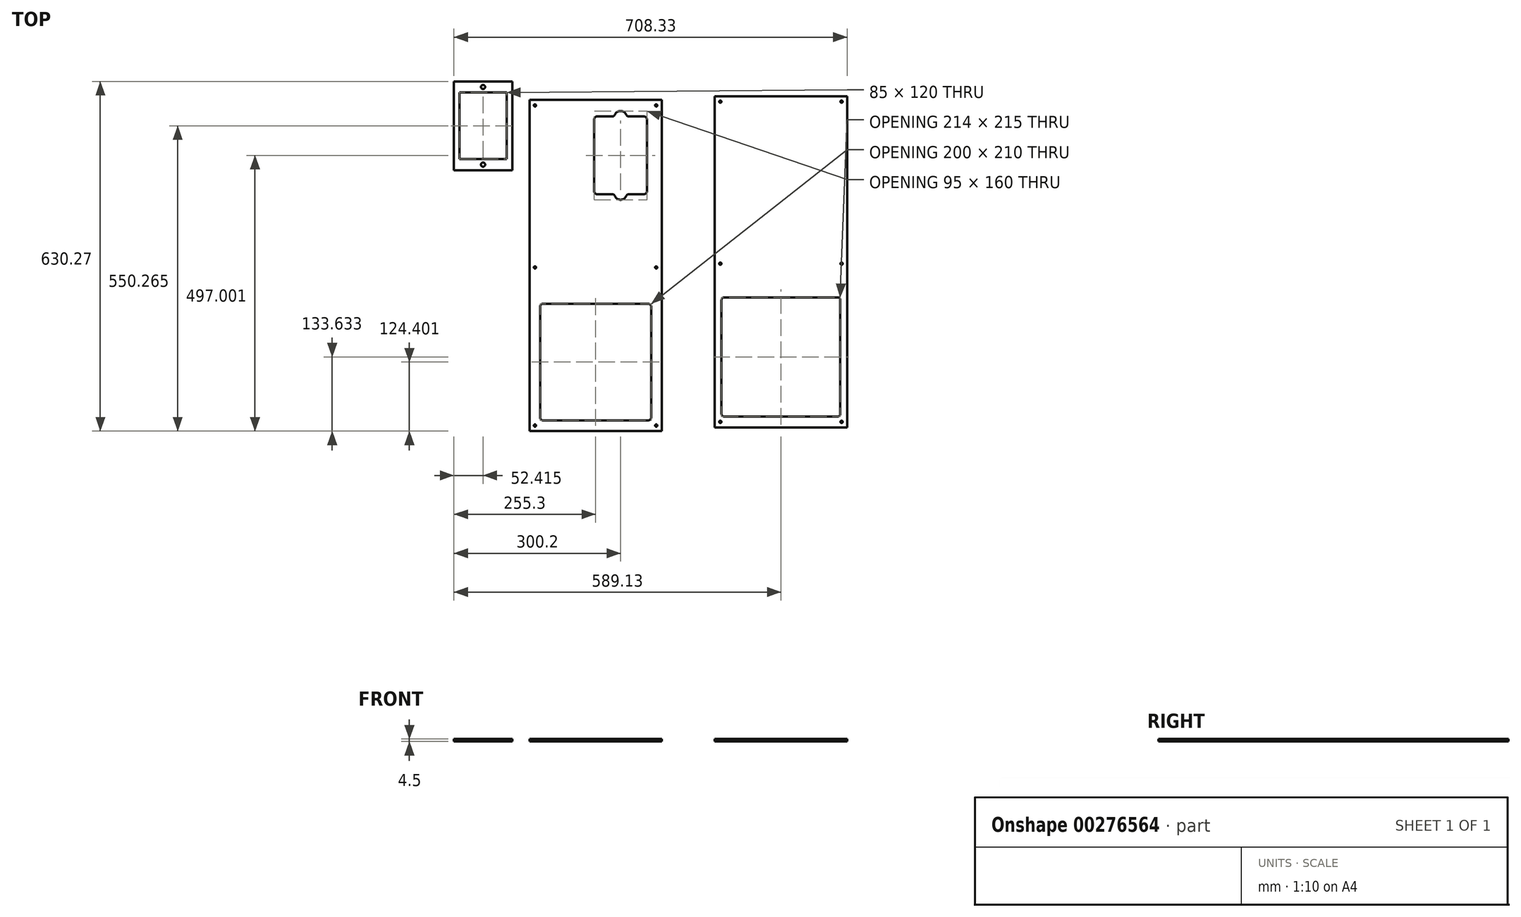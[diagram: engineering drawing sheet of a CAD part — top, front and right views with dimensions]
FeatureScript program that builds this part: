
annotation { "Feature Type Name" : "Feature", "Feature Type Description" : "" }
export const myFeature = defineFeature(function(context is Context, id is Id, definition is map)
    precondition{}
    {
        {
            var Q0;
            Q0=qCreatedBy(makeId("Top.planeOp"),FACE);
            var sketch = newSketch(context, id + "F0", { "sketchPlane" : qUnion([Q0])});
            skLineSegment(sketch, "E0.bottom", {"start": v(-206, 398.8) * mm, "end": v(32.4, 398.8) * mm});
            skLineSegment(sketch, "E0.top", {"start": v(-206, -198.2) * mm, "end": v(32.4, -198.2) * mm});
            skLineSegment(sketch, "E0.left", {"start": v(-206, 398.8) * mm, "end": v(-206, -198.2) * mm});
            skLineSegment(sketch, "E0.right", {"start": v(32.4, 398.8) * mm, "end": v(32.4, -198.2) * mm});
            skLineSegment(sketch, "E1.bottom", {"start": v(-186.8, 31.2) * mm, "end": v(13.2, 31.2) * mm});
            skLineSegment(sketch, "E1.top", {"start": v(-186.8, -178.8) * mm, "end": v(13.2, -178.8) * mm});
            skLineSegment(sketch, "E1.left", {"start": v(-186.8, 31.2) * mm, "end": v(-186.8, -178.8) * mm});
            skLineSegment(sketch, "E1.right", {"start": v(13.2, 31.2) * mm, "end": v(13.2, -178.8) * mm});
            skLineSegment(sketch, "E2.bottom", {"start": v(-89.4, 368.8) * mm, "end": v(5.6, 368.8) * mm});
            skLineSegment(sketch, "E2.top", {"start": v(-89.4, 228.8) * mm, "end": v(5.6, 228.8) * mm});
            skLineSegment(sketch, "E2.left", {"start": v(-89.4, 368.8) * mm, "end": v(-89.4, 228.8) * mm});
            skLineSegment(sketch, "E2.right", {"start": v(5.6, 368.8) * mm, "end": v(5.6, 228.8) * mm});
            skCircle(sketch, "E3", {"center": v(-49.48, 368.8) * mm, "radius": 3.2 * mm});
            skSolve(sketch);
        }
        {
            var Q0;
            Q0 = qSketchRegion(id + "F0", true);
            extrude(context, id + "F1", {"entities" : qUnion([Q0]), "depth" : 4.5 * mm, "offsetDistance" : 25 * mm});
        }
        {
            var Q0;
            Q0=makeQuery(id+"F1.opExtrude","CAP_FACE",FACE,{"disambiguationData":[OSD([sQuery(id+"F0.wireOp",EDGE,"E0.bottom"),sQuery(id+"F0.wireOp",EDGE,"E0.top"),sQuery(id+"F0.wireOp",EDGE,"E0.left"),sQuery(id+"F0.wireOp",EDGE,"E0.right"),sQuery(id+"F0.wireOp",EDGE,"E1.bottom"),sQuery(id+"F0.wireOp",EDGE,"E1.top"),sQuery(id+"F0.wireOp",EDGE,"E1.left"),sQuery(id+"F0.wireOp",EDGE,"E1.right"),sQuery(id+"F0.wireOp",EDGE,"E2.bottom"),sQuery(id+"F0.wireOp",EDGE,"E2.top"),sQuery(id+"F0.wireOp",EDGE,"E2.left"),sQuery(id+"F0.wireOp",EDGE,"E2.right"),sQuery(id+"F0.wireOp",EDGE,"f5iPQAOY-qOqS-fJNy-qLz2-Z3B5W6fyXTsv"),sQuery(id+"F0.wireOp",EDGE,"IoBfbX9C-VoXT-43uz-JrJR-B73ar7WCOE58")])],"isStart":false});
            var sketch = newSketch(context, id + "F2", { "sketchPlane" : qUnion([Q0])});
            skPoint(sketch, "E4", {"position": v(-196, -188.2) * mm});
            skPoint(sketch, "E5", {"position": v(22.4, -188.2) * mm});
            skPoint(sketch, "E6", {"position": v(22.4, 96.8) * mm});
            skPoint(sketch, "E7", {"position": v(22.4, 388.8) * mm});
            skPoint(sketch, "E8", {"position": v(-196, 96.8) * mm});
            skPoint(sketch, "E9", {"position": v(-196, 388.8) * mm});
            skSolve(sketch);
        }
        {
            var Q0;
            Q0=sQuery(id+"F2.wireOp",VERTEX,"E9");
            var Q1;
            Q1=sQuery(id+"F2.wireOp",VERTEX,"E7");
            var Q2;
            Q2=sQuery(id+"F2.wireOp",VERTEX,"E6");
            var Q3;
            Q3=sQuery(id+"F2.wireOp",VERTEX,"E8");
            var Q4;
            Q4=sQuery(id+"F2.wireOp",VERTEX,"E4");
            var Q5;
            Q5=sQuery(id+"F2.wireOp",VERTEX,"E5");
            var Q6;
            Q6=makeQuery(id+"F1.opExtrude","SWEPT_BODY",BODY,{"disambiguationData":[OSD([sQuery(id+"F0.wireOp",EDGE,"E0.bottom"),sQuery(id+"F0.wireOp",EDGE,"E0.top"),sQuery(id+"F0.wireOp",EDGE,"E0.left"),sQuery(id+"F0.wireOp",EDGE,"E0.right"),sQuery(id+"F0.wireOp",EDGE,"E1.bottom"),sQuery(id+"F0.wireOp",EDGE,"E1.top"),sQuery(id+"F0.wireOp",EDGE,"E1.left"),sQuery(id+"F0.wireOp",EDGE,"E1.right"),sQuery(id+"F0.wireOp",EDGE,"E2.bottom"),sQuery(id+"F0.wireOp",EDGE,"E2.top"),sQuery(id+"F0.wireOp",EDGE,"E2.left"),sQuery(id+"F0.wireOp",EDGE,"E2.right"),sQuery(id+"F0.wireOp",EDGE,"f5iPQAOY-qOqS-fJNy-qLz2-Z3B5W6fyXTsv"),sQuery(id+"F0.wireOp",EDGE,"IoBfbX9C-VoXT-43uz-JrJR-B73ar7WCOE58")])]});
            hole(context, id + "F3", {"style" : HoleStyle.SIMPLE, "endStyle" : HoleEndStyle.THROUGH, "holeDiameter" : 4 * mm, "majorDiameter" : 5 * mm, "tappedDepth" : 12 * mm, "tapClearance" : 3, "locations" : qUnion([Q0, Q1, Q2, Q3, Q4, Q5]), "scope" : qUnion([Q6])});
        }
        {
            var Q0;
            Q0=qCreatedBy(makeId("Top.planeOp"),FACE);
            var sketch = newSketch(context, id + "F4", { "sketchPlane" : qUnion([Q0])});
            skLineSegment(sketch, "E10.bottom", {"start": v(127.83, 405.53) * mm, "end": v(366.23, 405.53) * mm});
            skLineSegment(sketch, "E10.top", {"start": v(127.83, -191.47) * mm, "end": v(366.23, -191.47) * mm});
            skLineSegment(sketch, "E10.left", {"start": v(127.83, 405.53) * mm, "end": v(127.83, -191.47) * mm});
            skLineSegment(sketch, "E10.right", {"start": v(366.23, 405.53) * mm, "end": v(366.23, -191.47) * mm});
            skLineSegment(sketch, "E11.bottom", {"start": v(140.03, 42.93) * mm, "end": v(354.03, 42.93) * mm});
            skLineSegment(sketch, "E11.top", {"start": v(140.03, -172.07) * mm, "end": v(354.03, -172.07) * mm});
            skLineSegment(sketch, "E11.left", {"start": v(140.03, 42.93) * mm, "end": v(140.03, -172.07) * mm});
            skLineSegment(sketch, "E11.right", {"start": v(354.03, 42.93) * mm, "end": v(354.03, -172.07) * mm});
            skPoint(sketch, "E12", {"position": v(137.83, 103.53) * mm});
            skSolve(sketch);
        }
        {
            var Q0;
            Q0 = qSketchRegion(id + "F4", true);
            extrude(context, id + "F5", {"entities" : qUnion([Q0]), "depth" : 4.5 * mm, "offsetDistance" : 25 * mm});
        }
        {
            var Q0;
            Q0=makeQuery(id+"F5.opExtrude","CAP_FACE",FACE,{"disambiguationData":[OSD([sQuery(id+"F4.wireOp",EDGE,"E10.bottom"),sQuery(id+"F4.wireOp",EDGE,"E10.top"),sQuery(id+"F4.wireOp",EDGE,"E10.left"),sQuery(id+"F4.wireOp",EDGE,"E10.right"),sQuery(id+"F4.wireOp",EDGE,"E11.bottom"),sQuery(id+"F4.wireOp",EDGE,"E11.top"),sQuery(id+"F4.wireOp",EDGE,"E11.left"),sQuery(id+"F4.wireOp",EDGE,"E11.right")])],"isStart":false});
            var sketch = newSketch(context, id + "F6", { "sketchPlane" : qUnion([Q0])});
            skPoint(sketch, "E13", {"position": v(137.83, 395.53) * mm});
            skPoint(sketch, "E14", {"position": v(356.23, 395.53) * mm});
            skPoint(sketch, "E15", {"position": v(356.23, 103.53) * mm});
            skPoint(sketch, "E16", {"position": v(356.23, -181.47) * mm});
            skPoint(sketch, "E17", {"position": v(137.83, -181.47) * mm});
            skPoint(sketch, "E18", {"position": v(137.83, 103.53) * mm});
            skSolve(sketch);
        }
        {
            var Q0;
            Q0=sQuery(id+"F6.wireOp",VERTEX,"E13");
            var Q1;
            Q1=sQuery(id+"F6.wireOp",VERTEX,"E14");
            var Q2;
            Q2=sQuery(id+"F6.wireOp",VERTEX,"E15");
            var Q3;
            Q3=sQuery(id+"F6.wireOp",VERTEX,"E18");
            var Q4;
            Q4=sQuery(id+"F6.wireOp",VERTEX,"E17");
            var Q5;
            Q5=sQuery(id+"F6.wireOp",VERTEX,"E16");
            var Q6;
            Q6=makeQuery(id+"F5.opExtrude","SWEPT_BODY",BODY,{"disambiguationData":[OSD([sQuery(id+"F4.wireOp",EDGE,"E10.bottom"),sQuery(id+"F4.wireOp",EDGE,"E10.top"),sQuery(id+"F4.wireOp",EDGE,"E10.left"),sQuery(id+"F4.wireOp",EDGE,"E10.right"),sQuery(id+"F4.wireOp",EDGE,"E11.bottom"),sQuery(id+"F4.wireOp",EDGE,"E11.top"),sQuery(id+"F4.wireOp",EDGE,"E11.left"),sQuery(id+"F4.wireOp",EDGE,"E11.right")])]});
            hole(context, id + "F7", {"style" : HoleStyle.SIMPLE, "endStyle" : HoleEndStyle.THROUGH, "holeDiameter" : 4 * mm, "majorDiameter" : 5 * mm, "tappedDepth" : 12 * mm, "tapClearance" : 3, "locations" : qUnion([Q0, Q1, Q2, Q3, Q4, Q5]), "scope" : qUnion([Q6])});
        }
        {
            var Q0;
            Q0=makeQuery(id+"F5.opExtrude","SWEPT_EDGE",EDGE,{"disambiguationData":[OSD([sQuery(id+"F4.wireOp",EDGE,"E11.bottom"),sQuery(id+"F4.wireOp",EDGE,"E11.right")])]});
            var Q1;
            Q1=makeQuery(id+"F5.opExtrude","SWEPT_EDGE",EDGE,{"disambiguationData":[OSD([sQuery(id+"F4.wireOp",EDGE,"E11.bottom"),sQuery(id+"F4.wireOp",EDGE,"E11.left")])]});
            var Q2;
            Q2=makeQuery(id+"F5.opExtrude","SWEPT_EDGE",EDGE,{"disambiguationData":[OSD([sQuery(id+"F4.wireOp",EDGE,"E11.top"),sQuery(id+"F4.wireOp",EDGE,"E11.right")])]});
            var Q3;
            Q3=makeQuery(id+"F5.opExtrude","SWEPT_EDGE",EDGE,{"disambiguationData":[OSD([sQuery(id+"F4.wireOp",EDGE,"E11.top"),sQuery(id+"F4.wireOp",EDGE,"E11.left")])]});
            fillet(context, id + "F8", {"entities" : qUnion([Q0, Q1, Q2, Q3]), "radius" : 5 * mm, "tangentPropagation" : true, "allowEdgeOverflow" : false});
        }
        {
            var Q0;
            Q0=makeQuery(id+"F1.opExtrude","SWEPT_EDGE",EDGE,{"disambiguationData":[OSD([sQuery(id+"F0.wireOp",EDGE,"E1.bottom"),sQuery(id+"F0.wireOp",EDGE,"E1.right")])]});
            var Q1;
            Q1=makeQuery(id+"F1.opExtrude","SWEPT_EDGE",EDGE,{"disambiguationData":[OSD([sQuery(id+"F0.wireOp",EDGE,"E1.bottom"),sQuery(id+"F0.wireOp",EDGE,"E1.left")])]});
            var Q2;
            Q2=makeQuery(id+"F1.opExtrude","SWEPT_EDGE",EDGE,{"disambiguationData":[OSD([sQuery(id+"F0.wireOp",EDGE,"E1.top"),sQuery(id+"F0.wireOp",EDGE,"E1.right")])]});
            var Q3;
            Q3=makeQuery(id+"F1.opExtrude","SWEPT_EDGE",EDGE,{"disambiguationData":[OSD([sQuery(id+"F0.wireOp",EDGE,"E1.top"),sQuery(id+"F0.wireOp",EDGE,"E1.left")])]});
            fillet(context, id + "F9", {"entities" : qUnion([Q0, Q1, Q2, Q3]), "radius" : 5 * mm, "tangentPropagation" : true, "allowEdgeOverflow" : false});
        }
        {
            var Q0;
            Q0=makeQuery(id+"F1.opExtrude","SWEPT_EDGE",EDGE,{"disambiguationData":[OSD([sQuery(id+"F0.wireOp",EDGE,"E2.bottom"),sQuery(id+"F0.wireOp",EDGE,"E2.left")])]});
            var Q1;
            Q1=makeQuery(id+"F1.opExtrude","SWEPT_EDGE",EDGE,{"disambiguationData":[OSD([sQuery(id+"F0.wireOp",EDGE,"E2.bottom"),sQuery(id+"F0.wireOp",EDGE,"E2.right")])]});
            var Q2;
            Q2=makeQuery(id+"F1.opExtrude","SWEPT_EDGE",EDGE,{"disambiguationData":[OSD([sQuery(id+"F0.wireOp",EDGE,"E2.top"),sQuery(id+"F0.wireOp",EDGE,"E2.right")])]});
            var Q3;
            Q3=makeQuery(id+"F1.opExtrude","SWEPT_EDGE",EDGE,{"disambiguationData":[OSD([sQuery(id+"F0.wireOp",EDGE,"E2.top"),sQuery(id+"F0.wireOp",EDGE,"E2.left")])]});
            fillet(context, id + "F10", {"entities" : qUnion([Q0, Q1, Q2, Q3]), "tangentPropagation" : true, "radius" : 5 * mm, "defaultsChanged" : false, "vertexSettings" : [], "allowEdgeOverflow" : false});
        }
        {
            var Q0;
            Q0=qCreatedBy(makeId("Top.planeOp"),FACE);
            var sketch = newSketch(context, id + "F11", { "sketchPlane" : qUnion([Q0])});
            skLineSegment(sketch, "E19.bottom", {"start": v(-342.1, 432.07) * mm, "end": v(-237.1, 432.07) * mm});
            skLineSegment(sketch, "E19.top", {"start": v(-342.1, 272.07) * mm, "end": v(-237.1, 272.07) * mm});
            skLineSegment(sketch, "E19.left", {"start": v(-342.1, 432.07) * mm, "end": v(-342.1, 272.07) * mm});
            skLineSegment(sketch, "E19.right", {"start": v(-237.1, 432.07) * mm, "end": v(-237.1, 272.07) * mm});
            skSolve(sketch);
        }
        {
            var Q0;
            Q0=makeQuery(id+"F11.imprint","IMPRINT",FACE,{"disambiguationData":[TD([[makeQuery(id+"F11.imprint","IMPRINT",EDGE,{"derivedFrom":sQuery(id+"F11.wireOp",EDGE,"E19.bottom")}),-1.0]])]});
            extrude(context, id + "F12", {"entities" : qUnion([Q0]), "depth" : 4.5 * mm, "offsetDistance" : 25 * mm});
        }
        {
            var Q0;
            Q0=makeQuery(id+"F12.opExtrude","CAP_FACE",FACE,{"disambiguationData":[OSD([sQuery(id+"F11.wireOp",EDGE,"E19.bottom"),sQuery(id+"F11.wireOp",EDGE,"E19.top"),sQuery(id+"F11.wireOp",EDGE,"E19.left"),sQuery(id+"F11.wireOp",EDGE,"E19.right")])],"isStart":false});
            var sketch = newSketch(context, id + "F13", { "sketchPlane" : qUnion([Q0])});
            skLineSegment(sketch, "E20.bottom", {"start": v(-332.18, 412.07) * mm, "end": v(-247.18, 412.07) * mm});
            skLineSegment(sketch, "E20.top", {"start": v(-332.18, 292.07) * mm, "end": v(-247.18, 292.07) * mm});
            skLineSegment(sketch, "E20.left", {"start": v(-332.18, 412.07) * mm, "end": v(-332.18, 292.07) * mm});
            skLineSegment(sketch, "E20.right", {"start": v(-247.18, 412.07) * mm, "end": v(-247.18, 292.07) * mm});
            skCircle(sketch, "E21", {"center": v(-289.6, 422.07) * mm, "radius": 3.75 * mm});
            skPoint(sketch, "E21.centerSnap0", {"position": v(-289.6, 432.07) * mm});
            skCircle(sketch, "E22", {"center": v(-289.6, 282.07) * mm, "radius": 3.75 * mm});
            skSolve(sketch);
        }
        {
            var Q0;
            Q0 = qSketchRegion(id + "F13", true);
            extrude(context, id + "F14", {"entities" : qUnion([Q0]), "operationType" : NewBodyOperationType.REMOVE, "oppositeDirection" : true, "depth" : 25 * mm, "offsetDistance" : 25 * mm});
        }
        {
            var Q0;
            Q0=makeQuery(id+"F1.opExtrude","CAP_FACE",FACE,{"disambiguationData":[OSD([sQuery(id+"F0.wireOp",EDGE,"E0.bottom"),sQuery(id+"F0.wireOp",EDGE,"E0.top"),sQuery(id+"F0.wireOp",EDGE,"E0.left"),sQuery(id+"F0.wireOp",EDGE,"E0.right"),sQuery(id+"F0.wireOp",EDGE,"E1.bottom"),sQuery(id+"F0.wireOp",EDGE,"E1.top"),sQuery(id+"F0.wireOp",EDGE,"E1.left"),sQuery(id+"F0.wireOp",EDGE,"E1.right"),sQuery(id+"F0.wireOp",EDGE,"E2.bottom"),sQuery(id+"F0.wireOp",EDGE,"E2.top"),sQuery(id+"F0.wireOp",EDGE,"E2.left"),sQuery(id+"F0.wireOp",EDGE,"E2.right"),sQuery(id+"F0.wireOp",EDGE,"E3")])],"isStart":false});
            var sketch = newSketch(context, id + "F15", { "sketchPlane" : qUnion([Q0])});
            skLineSegment(sketch, "E23.bottom", {"start": v(-52.9, 378.8) * mm, "end": v(-30.9, 378.8) * mm});
            skLineSegment(sketch, "E23.top", {"start": v(-52.9, 218.8) * mm, "end": v(-30.9, 218.8) * mm});
            skLineSegment(sketch, "E23.left", {"start": v(-52.9, 378.8) * mm, "end": v(-52.9, 218.8) * mm});
            skLineSegment(sketch, "E23.right", {"start": v(-30.9, 378.8) * mm, "end": v(-30.9, 218.8) * mm});
            skSolve(sketch);
        }
        {
            var Q0;
            Q0 = qSketchRegion(id + "F15", true);
            extrude(context, id + "F16", {"entities" : qUnion([Q0]), "operationType" : NewBodyOperationType.REMOVE, "oppositeDirection" : true, "depth" : 25 * mm, "offsetDistance" : 25 * mm});
        }
        {
            var Q0;
            Q0=makeQuery(id+"F16.boolean.opBoolean","COPY",EDGE,{"derivedFrom":makeQuery(id+"F16.opExtrude","SWEPT_EDGE",EDGE,{"disambiguationData":[OSD([sQuery(id+"F15.wireOp",EDGE,"E23.bottom"),sQuery(id+"F15.wireOp",EDGE,"E23.right")])]})});
            var Q1;
            Q1=makeQuery(id+"F16.boolean.opBoolean","COPY",EDGE,{"derivedFrom":makeQuery(id+"F16.opExtrude","SWEPT_EDGE",EDGE,{"disambiguationData":[OSD([sQuery(id+"F15.wireOp",EDGE,"E23.bottom"),sQuery(id+"F15.wireOp",EDGE,"E23.left")])]})});
            var Q2;
            Q2=makeQuery(id+"F16.boolean.opBoolean","COPY",EDGE,{"derivedFrom":makeQuery(id+"F16.opExtrude","SWEPT_EDGE",EDGE,{"disambiguationData":[OSD([sQuery(id+"F15.wireOp",EDGE,"E23.top"),sQuery(id+"F15.wireOp",EDGE,"E23.left")])]})});
            var Q3;
            Q3=makeQuery(id+"F16.boolean.opBoolean","COPY",EDGE,{"derivedFrom":makeQuery(id+"F16.opExtrude","SWEPT_EDGE",EDGE,{"disambiguationData":[OSD([sQuery(id+"F15.wireOp",EDGE,"E23.top"),sQuery(id+"F15.wireOp",EDGE,"E23.right")])]})});
            fillet(context, id + "F17", {"entities" : qUnion([Q0, Q1, Q2, Q3]), "tangentPropagation" : true, "radius" : 11 * mm, "defaultsChanged" : true, "vertexSettings" : [], "allowEdgeOverflow" : false});
        }
        {
            var Q0;
            {var subQ4=sQuery(id+"F0.wireOp",EDGE,"E2.bottom");var subQ13=sQuery(id+"F15.wireOp",EDGE,"E23.left");Q0=makeQuery(id+"F17.opFillet","BLEND_EDGE",EDGE,{"blendedFrom":[makeQuery(id+"F16.boolean.opBoolean","COPY",EDGE,{"derivedFrom":makeQuery(id+"F16.opExtrude","SWEPT_EDGE",EDGE,{"disambiguationData":[OSD([sQuery(id+"F15.wireOp",EDGE,"E23.bottom"),subQ13])]})}),makeQuery(id+"F16.boolean.opBoolean","SPLIT",FACE,{"disambiguationData":[TD([makeQuery(id+"F16.opExtrude","SWEPT_FACE",FACE,{"disambiguationData":[OSD([subQ13])]})])],"derivedFrom":makeQuery(id+"F1.opExtrude","SWEPT_FACE",FACE,{"disambiguationData":[OSD([subQ4])]})})],"blendedInto":[makeQuery(id+"F16.boolean.opBoolean","SPLIT",FACE,{"disambiguationData":[TD([makeQuery(id+"F16.opExtrude","SWEPT_FACE",FACE,{"disambiguationData":[OSD([subQ13])]})])],"derivedFrom":makeQuery(id+"F1.opExtrude","SWEPT_FACE",FACE,{"disambiguationData":[OSD([subQ4])]})})]});}
            var Q1;
            {var subQ4=sQuery(id+"F0.wireOp",EDGE,"E2.bottom");var subQ13=sQuery(id+"F15.wireOp",EDGE,"E23.right");Q1=makeQuery(id+"F17.opFillet","BLEND_EDGE",EDGE,{"blendedFrom":[makeQuery(id+"F16.boolean.opBoolean","COPY",EDGE,{"derivedFrom":makeQuery(id+"F16.opExtrude","SWEPT_EDGE",EDGE,{"disambiguationData":[OSD([sQuery(id+"F15.wireOp",EDGE,"E23.bottom"),subQ13])]})}),makeQuery(id+"F16.boolean.opBoolean","SPLIT",FACE,{"disambiguationData":[TD([makeQuery(id+"F16.opExtrude","SWEPT_FACE",FACE,{"disambiguationData":[OSD([subQ13])]})])],"derivedFrom":makeQuery(id+"F1.opExtrude","SWEPT_FACE",FACE,{"disambiguationData":[OSD([subQ4])]})})],"blendedInto":[makeQuery(id+"F16.boolean.opBoolean","SPLIT",FACE,{"disambiguationData":[TD([makeQuery(id+"F16.opExtrude","SWEPT_FACE",FACE,{"disambiguationData":[OSD([subQ13])]})])],"derivedFrom":makeQuery(id+"F1.opExtrude","SWEPT_FACE",FACE,{"disambiguationData":[OSD([subQ4])]})})]});}
            var Q2;
            {var subQ3=sQuery(id+"F0.wireOp",EDGE,"E2.top");var subQ13=sQuery(id+"F15.wireOp",EDGE,"E23.right");Q2=makeQuery(id+"F17.opFillet","BLEND_EDGE",EDGE,{"blendedFrom":[makeQuery(id+"F16.boolean.opBoolean","COPY",EDGE,{"derivedFrom":makeQuery(id+"F16.opExtrude","SWEPT_EDGE",EDGE,{"disambiguationData":[OSD([sQuery(id+"F15.wireOp",EDGE,"E23.top"),subQ13])]})}),makeQuery(id+"F16.boolean.opBoolean","SPLIT",FACE,{"disambiguationData":[TD([makeQuery(id+"F16.opExtrude","SWEPT_FACE",FACE,{"disambiguationData":[OSD([subQ13])]})])],"derivedFrom":makeQuery(id+"F1.opExtrude","SWEPT_FACE",FACE,{"disambiguationData":[OSD([subQ3])]})})],"blendedInto":[makeQuery(id+"F16.boolean.opBoolean","SPLIT",FACE,{"disambiguationData":[TD([makeQuery(id+"F16.opExtrude","SWEPT_FACE",FACE,{"disambiguationData":[OSD([subQ13])]})])],"derivedFrom":makeQuery(id+"F1.opExtrude","SWEPT_FACE",FACE,{"disambiguationData":[OSD([subQ3])]})})]});}
            var Q3;
            {var subQ3=sQuery(id+"F0.wireOp",EDGE,"E2.top");var subQ13=sQuery(id+"F15.wireOp",EDGE,"E23.left");Q3=makeQuery(id+"F17.opFillet","BLEND_EDGE",EDGE,{"blendedFrom":[makeQuery(id+"F16.boolean.opBoolean","COPY",EDGE,{"derivedFrom":makeQuery(id+"F16.opExtrude","SWEPT_EDGE",EDGE,{"disambiguationData":[OSD([sQuery(id+"F15.wireOp",EDGE,"E23.top"),subQ13])]})}),makeQuery(id+"F16.boolean.opBoolean","SPLIT",FACE,{"disambiguationData":[TD([makeQuery(id+"F16.opExtrude","SWEPT_FACE",FACE,{"disambiguationData":[OSD([subQ13])]})])],"derivedFrom":makeQuery(id+"F1.opExtrude","SWEPT_FACE",FACE,{"disambiguationData":[OSD([subQ3])]})})],"blendedInto":[makeQuery(id+"F16.boolean.opBoolean","SPLIT",FACE,{"disambiguationData":[TD([makeQuery(id+"F16.opExtrude","SWEPT_FACE",FACE,{"disambiguationData":[OSD([subQ13])]})])],"derivedFrom":makeQuery(id+"F1.opExtrude","SWEPT_FACE",FACE,{"disambiguationData":[OSD([subQ3])]})})]});}
            fillet(context, id + "F18", {"entities" : qUnion([Q0, Q1, Q2, Q3]), "tangentPropagation" : true, "radius" : 5 * mm, "defaultsChanged" : false, "vertexSettings" : [], "allowEdgeOverflow" : false});
        }
    });
